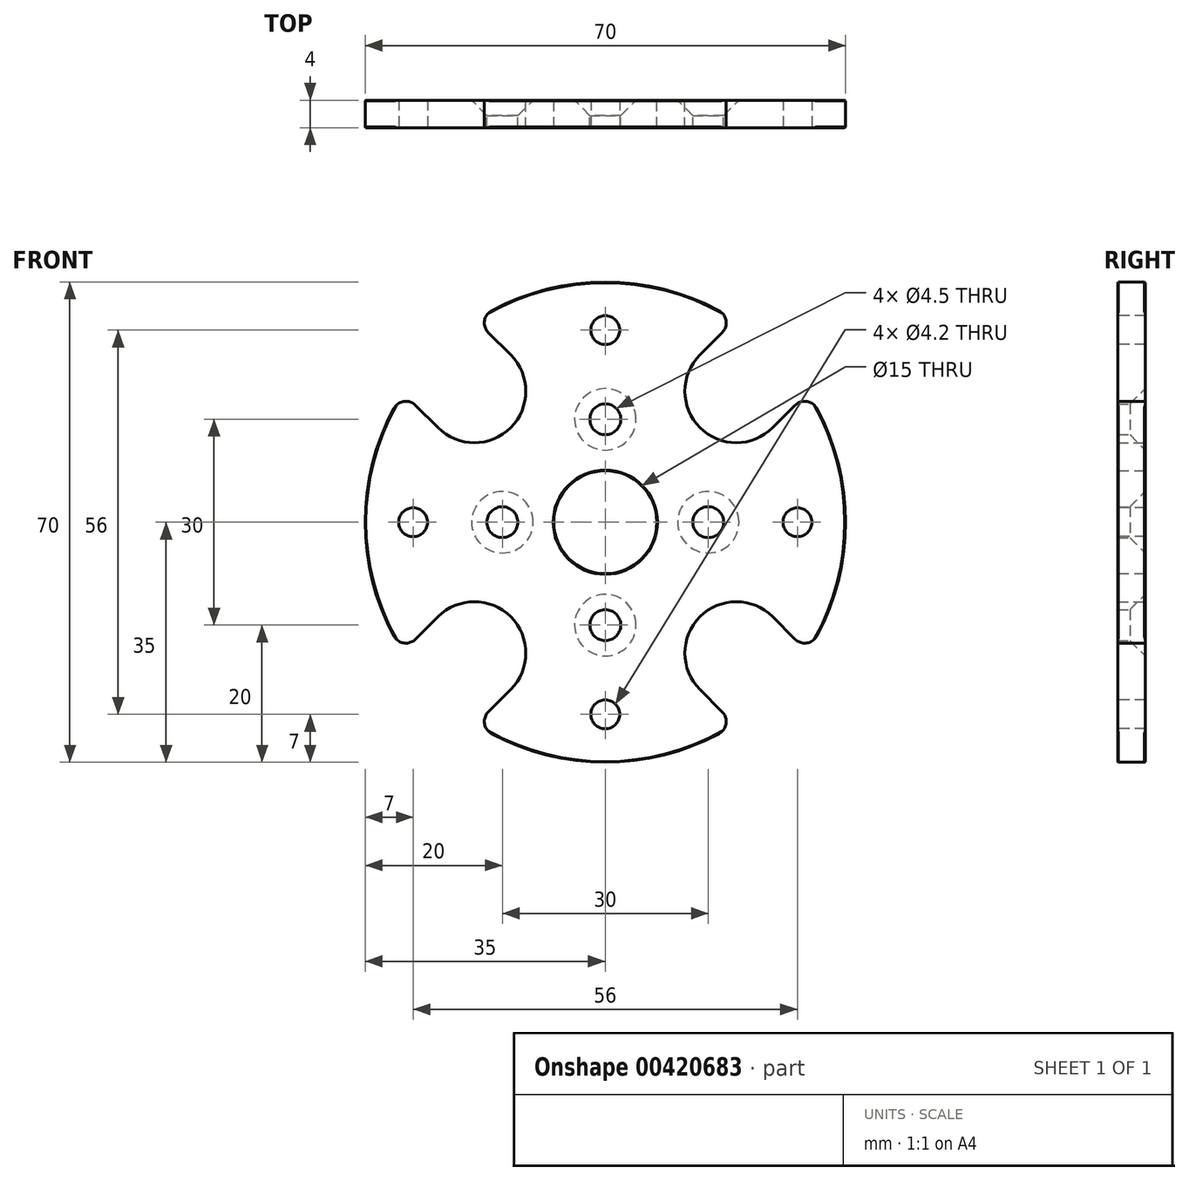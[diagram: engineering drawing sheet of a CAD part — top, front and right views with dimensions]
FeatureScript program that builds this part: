
annotation { "Feature Type Name" : "Feature", "Feature Type Description" : "" }
export const myFeature = defineFeature(function(context is Context, id is Id, definition is map)
    precondition{}
    {
        {
            var Q0;
            Q0=qCreatedBy(makeId("Front.planeOp"),FACE);
            var sketch = newSketch(context, id + "F0", { "sketchPlane" : qUnion([Q0])});
            skCircle(sketch, "E0", {"center": v(0, 0) * mm, "radius": 35 * mm});
            skCircle(sketch, "E1", {"center": v(0, 0) * mm, "radius": 7.5 * mm});
            skSolve(sketch);
        }
        {
            var Q0;
            Q0 = qSketchRegion(id + "F0", true);
            extrude(context, id + "F1", {"entities" : qUnion([Q0]), "offsetDistance" : 25 * mm, "depth" : 4 * mm});
        }
        {
            var Q0;
            Q0=makeQuery(id+"F1.opExtrude","CAP_EDGE",EDGE,{"disambiguationData":[OSD([sQuery(id+"F0.wireOp",EDGE,"E0")])],"isStart":false});
            var Q1;
            Q1=makeQuery(id+"F1.opExtrude","CAP_EDGE",EDGE,{"disambiguationData":[OSD([sQuery(id+"F0.wireOp",EDGE,"E0")])],"isStart":true});
            var Q2;
            Q2=makeQuery(id+"F1.opExtrude","CAP_EDGE",EDGE,{"disambiguationData":[OSD([sQuery(id+"F0.wireOp",EDGE,"E1")])],"isStart":true});
            var Q3;
            Q3=makeQuery(id+"F1.opExtrude","CAP_EDGE",EDGE,{"disambiguationData":[OSD([sQuery(id+"F0.wireOp",EDGE,"E1")])],"isStart":false});
            var Q4;
            Q4=makeQuery(id+"F1.opExtrude","CAP_EDGE",EDGE,{"disambiguationData":[OSD([sQuery(id+"F0.wireOp",EDGE,"1tDVeXT1-AbAI-RyJg-cryw-dks7lifIOjR4")])],"isStart":true});
            var Q5;
            Q5=makeQuery(id+"F1.opExtrude","CAP_EDGE",EDGE,{"disambiguationData":[OSD([sQuery(id+"F0.wireOp",EDGE,"365fb698-64a0-40e7-aaef-e05ef07254d6.1.0")])],"isStart":true});
            var Q6;
            Q6=makeQuery(id+"F1.opExtrude","CAP_EDGE",EDGE,{"disambiguationData":[OSD([sQuery(id+"F0.wireOp",EDGE,"365fb698-64a0-40e7-aaef-e05ef07254d6.2.0")])],"isStart":true});
            var Q7;
            Q7=makeQuery(id+"F1.opExtrude","CAP_EDGE",EDGE,{"disambiguationData":[OSD([sQuery(id+"F0.wireOp",EDGE,"365fb698-64a0-40e7-aaef-e05ef07254d6.3.0")])],"isStart":true});
            chamfer(context, id + "F2", {"entities" : qUnion([Q0, Q1, Q2, Q3, Q4, Q5, Q6, Q7]), "width" : 0.1 * mm, "tangentPropagation" : true});
        }
        {
            var Q0;
            Q0=qCreatedBy(makeId("Front.planeOp"),FACE);
            var sketch = newSketch(context, id + "F3", { "sketchPlane" : qUnion([Q0])});
            skCircle(sketch, "E2", {"center": v(0, 0) * mm, "radius": 15 * mm, "construction": true});
            skPoint(sketch, "E3", {"position": v(0, 15) * mm});
            skPoint(sketch, "E4", {"position": v(0, -15) * mm});
            skPoint(sketch, "E5", {"position": v(15, 0) * mm});
            skPoint(sketch, "E6", {"position": v(-15, 0) * mm});
            skSolve(sketch);
        }
        {
            var Q0;
            Q0=sQuery(id+"F3.wireOp",VERTEX,"E6");
            var Q1;
            Q1=sQuery(id+"F3.wireOp",VERTEX,"E4");
            var Q2;
            Q2=sQuery(id+"F3.wireOp",VERTEX,"E5");
            var Q3;
            Q3=sQuery(id+"F3.wireOp",VERTEX,"E3");
            var Q4;
            Q4=makeQuery(id+"F1.opExtrude","SWEPT_BODY",BODY,{"disambiguationData":[OSD([sQuery(id+"F0.wireOp",EDGE,"E0"),sQuery(id+"F0.wireOp",EDGE,"E1")])]});
            hole(context, id + "F4", {"style" : HoleStyle.C_SINK, "endStyle" : HoleEndStyle.THROUGH, "oppositeDirection" : true, "standardTappedOrClearance" : lookupTablePath({ "fit" : "Normal", "standard" : "ISO", "size" : "M4", "type" : "Clearance" }), "standardBlindInLast" : lookupTablePath({ "fit" : "Normal", "standard" : "ISO", "engagement" : "75%", "pitch" : "0.7 mm", "size" : "M4", "type" : "Clearance & tapped" }), "holeDiameter" : 4.5 * mm, "cSinkDiameter" : 8.96 * mm, "cSinkAngle" : 90 * degree, "majorDiameter" : 5 * mm, "isTappedThrough" : true, "tappedDepth" : 12 * mm, "tapClearance" : 3, "locations" : qUnion([Q0, Q1, Q2, Q3]), "scope" : qUnion([Q4])});
        }
        {
            var Q0;
            Q0=makeQuery(id+"F1.opExtrude","CAP_FACE",FACE,{"disambiguationData":[OSD([sQuery(id+"F0.wireOp",EDGE,"E0"),sQuery(id+"F0.wireOp",EDGE,"E1")])],"isStart":true});
            var sketch = newSketch(context, id + "F5", { "sketchPlane" : qUnion([Q0])});
            skLineSegment(sketch, "E7", {"start": v(0, 0) * mm, "end": v(-41.26, -41.26) * mm, "construction": true});
            skArc(sketch, "E8", {"start": v(-13.79, -24.4) * mm, "mid": v(-13.79, -13.79) * mm, "end": v(-24.4, -13.79) * mm});
            skLineSegment(sketch, "E9", {"start": v(-13.79, -24.4) * mm, "end": v(-25.27, -35.87) * mm});
            skLineSegment(sketch, "E10", {"start": v(-25.27, -35.87) * mm, "end": v(-35.87, -25.27) * mm});
            skLineSegment(sketch, "E11", {"start": v(-35.87, -25.27) * mm, "end": v(-24.4, -13.79) * mm});
            skPoint(sketch, "E12.center", {"position": v(0, 0) * mm});
            skLineSegment(sketch, "E13.1.0", {"start": v(25.27, -35.87) * mm, "end": v(13.79, -24.4) * mm});
            skArc(sketch, "E13.1.1", {"start": v(24.4, -13.79) * mm, "mid": v(13.79, -13.79) * mm, "end": v(13.79, -24.4) * mm});
            skLineSegment(sketch, "E13.1.2", {"start": v(24.4, -13.79) * mm, "end": v(35.87, -25.27) * mm});
            skLineSegment(sketch, "E13.1.3", {"start": v(35.87, -25.27) * mm, "end": v(25.27, -35.87) * mm});
            skLineSegment(sketch, "E13.2.0", {"start": v(35.87, 25.27) * mm, "end": v(24.4, 13.79) * mm});
            skArc(sketch, "E13.2.1", {"start": v(13.79, 24.4) * mm, "mid": v(13.79, 13.79) * mm, "end": v(24.4, 13.79) * mm});
            skLineSegment(sketch, "E13.2.2", {"start": v(13.79, 24.4) * mm, "end": v(25.27, 35.87) * mm});
            skLineSegment(sketch, "E13.2.3", {"start": v(25.27, 35.87) * mm, "end": v(35.87, 25.27) * mm});
            skLineSegment(sketch, "E13.3.0", {"start": v(-25.27, 35.87) * mm, "end": v(-13.79, 24.4) * mm});
            skArc(sketch, "E13.3.1", {"start": v(-24.4, 13.79) * mm, "mid": v(-13.79, 13.79) * mm, "end": v(-13.79, 24.4) * mm});
            skLineSegment(sketch, "E13.3.2", {"start": v(-24.4, 13.79) * mm, "end": v(-35.87, 25.27) * mm});
            skLineSegment(sketch, "E13.3.3", {"start": v(-35.87, 25.27) * mm, "end": v(-25.27, 35.87) * mm});
            skSolve(sketch);
        }
        {
            var Q0;
            Q0 = qSketchRegion(id + "F5", true);
            var Q1;
            Q1=makeQuery(id+"F1.opExtrude","CAP_FACE",FACE,{"disambiguationData":[OSD([sQuery(id+"F0.wireOp",EDGE,"E0"),sQuery(id+"F0.wireOp",EDGE,"E1")])],"isStart":false});
            extrude(context, id + "F6", {"entities" : qUnion([Q0]), "operationType" : NewBodyOperationType.REMOVE, "endBound" : BoundingType.UP_TO_SURFACE, "oppositeDirection" : true, "depth" : 25 * mm, "endBoundEntityFace" : qUnion([Q1]), "offsetDistance" : 25 * mm});
        }
        {
            var Q0;
            Q0=makeQuery(id+"F6.boolean.opBoolean","INTERSECT",EDGE,{"derivedFrom":[makeQuery(id+"F1.opExtrude","SWEPT_FACE",FACE,{"disambiguationData":[OSD([sQuery(id+"F0.wireOp",EDGE,"E0")])]}),makeQuery(id+"F6.opExtrude","SWEPT_FACE",FACE,{"disambiguationData":[OSD([sQuery(id+"F5.wireOp",EDGE,"E11")])]})]});
            var Q1;
            Q1=makeQuery(id+"F6.boolean.opBoolean","INTERSECT",EDGE,{"derivedFrom":[makeQuery(id+"F1.opExtrude","SWEPT_FACE",FACE,{"disambiguationData":[OSD([sQuery(id+"F0.wireOp",EDGE,"E0")])]}),makeQuery(id+"F6.opExtrude","SWEPT_FACE",FACE,{"disambiguationData":[OSD([sQuery(id+"F5.wireOp",EDGE,"E9")])]})]});
            var Q2;
            Q2=makeQuery(id+"F6.boolean.opBoolean","INTERSECT",EDGE,{"derivedFrom":[makeQuery(id+"F1.opExtrude","SWEPT_FACE",FACE,{"disambiguationData":[OSD([sQuery(id+"F0.wireOp",EDGE,"E0")])]}),makeQuery(id+"F6.opExtrude","SWEPT_FACE",FACE,{"disambiguationData":[OSD([sQuery(id+"F5.wireOp",EDGE,"E13.1.0")])]})]});
            var Q3;
            Q3=makeQuery(id+"F6.boolean.opBoolean","INTERSECT",EDGE,{"derivedFrom":[makeQuery(id+"F1.opExtrude","SWEPT_FACE",FACE,{"disambiguationData":[OSD([sQuery(id+"F0.wireOp",EDGE,"E0")])]}),makeQuery(id+"F6.opExtrude","SWEPT_FACE",FACE,{"disambiguationData":[OSD([sQuery(id+"F5.wireOp",EDGE,"E13.1.2")])]})]});
            var Q4;
            Q4=makeQuery(id+"F6.boolean.opBoolean","INTERSECT",EDGE,{"derivedFrom":[makeQuery(id+"F1.opExtrude","SWEPT_FACE",FACE,{"disambiguationData":[OSD([sQuery(id+"F0.wireOp",EDGE,"E0")])]}),makeQuery(id+"F6.opExtrude","SWEPT_FACE",FACE,{"disambiguationData":[OSD([sQuery(id+"F5.wireOp",EDGE,"E13.2.0")])]})]});
            var Q5;
            Q5=makeQuery(id+"F6.boolean.opBoolean","INTERSECT",EDGE,{"derivedFrom":[makeQuery(id+"F1.opExtrude","SWEPT_FACE",FACE,{"disambiguationData":[OSD([sQuery(id+"F0.wireOp",EDGE,"E0")])]}),makeQuery(id+"F6.opExtrude","SWEPT_FACE",FACE,{"disambiguationData":[OSD([sQuery(id+"F5.wireOp",EDGE,"E13.2.2")])]})]});
            var Q6;
            Q6=makeQuery(id+"F6.boolean.opBoolean","INTERSECT",EDGE,{"derivedFrom":[makeQuery(id+"F1.opExtrude","SWEPT_FACE",FACE,{"disambiguationData":[OSD([sQuery(id+"F0.wireOp",EDGE,"E0")])]}),makeQuery(id+"F6.opExtrude","SWEPT_FACE",FACE,{"disambiguationData":[OSD([sQuery(id+"F5.wireOp",EDGE,"E13.3.0")])]})]});
            var Q7;
            Q7=makeQuery(id+"F6.boolean.opBoolean","INTERSECT",EDGE,{"derivedFrom":[makeQuery(id+"F1.opExtrude","SWEPT_FACE",FACE,{"disambiguationData":[OSD([sQuery(id+"F0.wireOp",EDGE,"E0")])]}),makeQuery(id+"F6.opExtrude","SWEPT_FACE",FACE,{"disambiguationData":[OSD([sQuery(id+"F5.wireOp",EDGE,"E13.3.2")])]})]});
            fillet(context, id + "F7", {"entities" : qUnion([Q0, Q1, Q2, Q3, Q4, Q5, Q6, Q7]), "tangentPropagation" : true, "radius" : 2 * mm, "defaultsChanged" : false, "vertexSettings" : [], "allowEdgeOverflow" : false});
        }
        {
            var Q0;
            Q0=makeQuery(id+"F1.opExtrude","CAP_FACE",FACE,{"disambiguationData":[OSD([sQuery(id+"F0.wireOp",EDGE,"E0"),sQuery(id+"F0.wireOp",EDGE,"E1")])],"isStart":false});
            var sketch = newSketch(context, id + "F8", { "sketchPlane" : qUnion([Q0])});
            skCircle(sketch, "E14", {"center": v(0, 0) * mm, "radius": 28 * mm, "construction": true});
            skPoint(sketch, "E15", {"position": v(0, 28) * mm});
            skPoint(sketch, "E16", {"position": v(28, 0) * mm});
            skPoint(sketch, "E17", {"position": v(0, -28) * mm});
            skPoint(sketch, "E18", {"position": v(-28, 0) * mm});
            skSolve(sketch);
        }
        {
            var Q0;
            Q0=sQuery(id+"F8.wireOp",VERTEX,"E15");
            var Q1;
            Q1=sQuery(id+"F8.wireOp",VERTEX,"E16");
            var Q2;
            Q2=sQuery(id+"F8.wireOp",VERTEX,"E17");
            var Q3;
            Q3=sQuery(id+"F8.wireOp",VERTEX,"E18");
            var Q4;
            Q4=makeQuery(id+"F1.opExtrude","SWEPT_BODY",BODY,{"disambiguationData":[OSD([sQuery(id+"F0.wireOp",EDGE,"E0"),sQuery(id+"F0.wireOp",EDGE,"E1")])]});
            hole(context, id + "F9", {"style" : HoleStyle.SIMPLE, "endStyle" : HoleEndStyle.THROUGH, "standardTappedOrClearance" : lookupTablePath({ "standard" : "ISO", "engagement" : "75%", "pitch" : "0.8 mm", "size" : "M5", "type" : "Tapped" }), "standardBlindInLast" : lookupTablePath({ "standard" : "ISO", "fit" : "Normal", "engagement" : "75%", "pitch" : "0.8 mm", "size" : "M5", "type" : "Clearance & tapped" }), "holeDiameter" : 4.2 * mm, "majorDiameter" : 5 * mm, "showTappedDepth" : true, "isTappedThrough" : true, "tappedDepth" : 12 * mm, "tapClearance" : 3, "locations" : qUnion([Q0, Q1, Q2, Q3]), "scope" : qUnion([Q4])});
        }
    });
